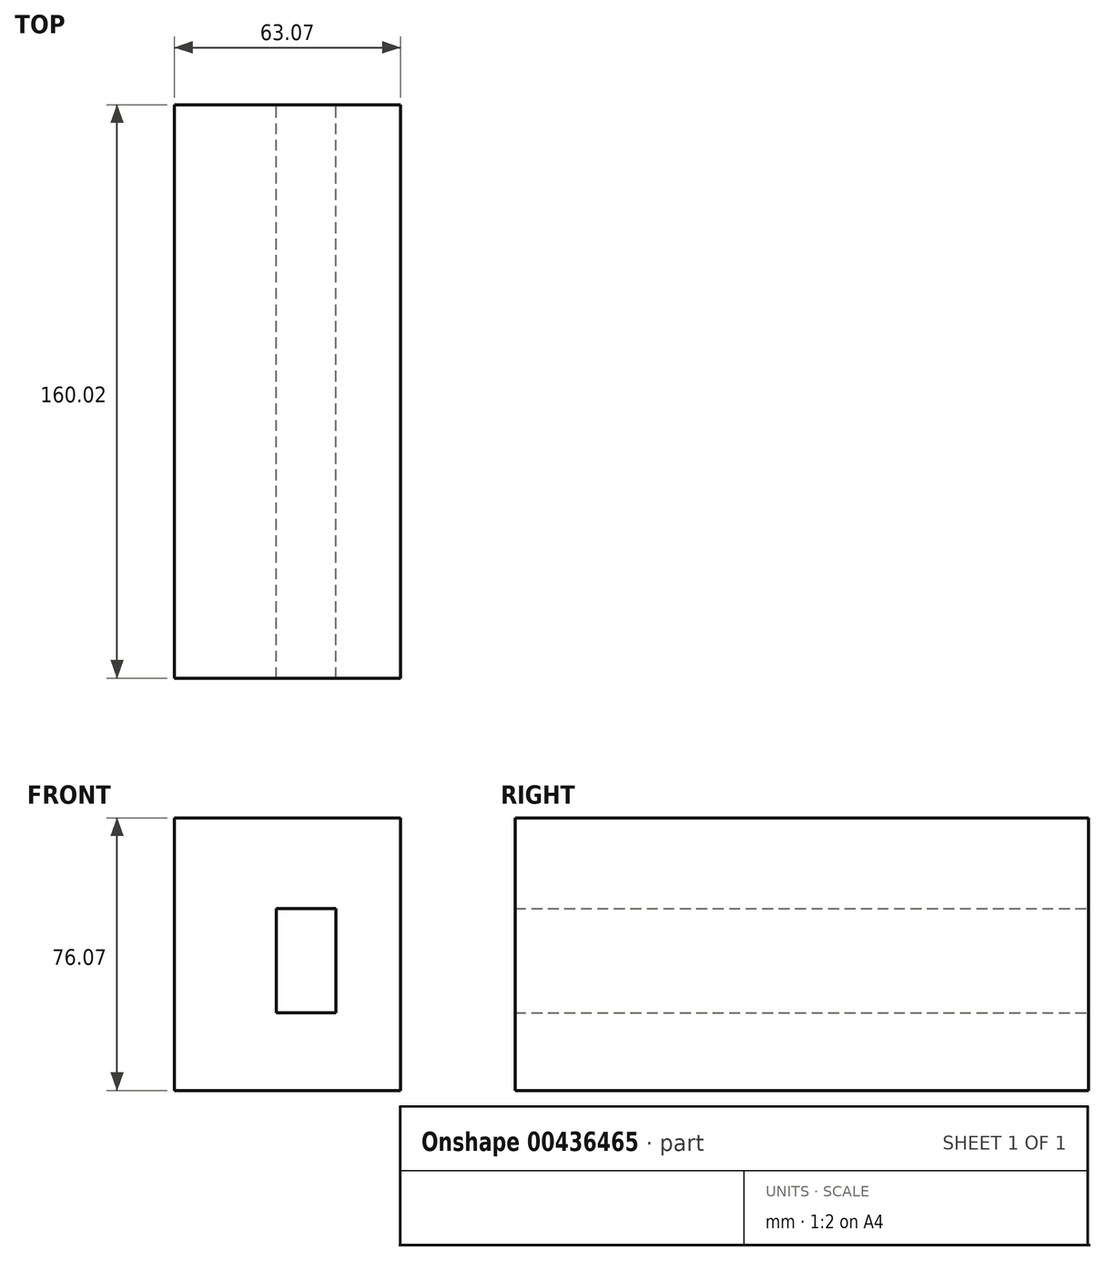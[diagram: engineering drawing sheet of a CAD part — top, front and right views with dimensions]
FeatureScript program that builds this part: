
annotation { "Feature Type Name" : "Feature", "Feature Type Description" : "" }
export const myFeature = defineFeature(function(context is Context, id is Id, definition is map)
    precondition{}
    {
        {
            var Q0;
            Q0=qCreatedBy(makeId("Front.planeOp"),FACE);
            var sketch = newSketch(context, id + "F0", { "sketchPlane" : qUnion([Q0])});
            skLineSegment(sketch, "E0.bottom", {"start": v(-45.1, 45.99) * mm, "end": v(17.97, 45.99) * mm});
            skLineSegment(sketch, "E0.top", {"start": v(-45.1, -30.08) * mm, "end": v(17.97, -30.08) * mm});
            skLineSegment(sketch, "E0.left", {"start": v(-45.1, 45.99) * mm, "end": v(-45.1, -30.08) * mm});
            skLineSegment(sketch, "E0.right", {"start": v(17.97, 45.99) * mm, "end": v(17.97, -30.08) * mm});
            skLineSegment(sketch, "E1.bottom", {"start": v(-16.62, 20.64) * mm, "end": v(0, 20.64) * mm});
            skLineSegment(sketch, "E1.top", {"start": v(-16.62, -8.38) * mm, "end": v(0, -8.38) * mm});
            skLineSegment(sketch, "E1.left", {"start": v(-16.62, 20.64) * mm, "end": v(-16.62, -8.38) * mm});
            skLineSegment(sketch, "E1.right", {"start": v(0, 20.64) * mm, "end": v(0, -8.38) * mm});
            skSolve(sketch);
        }
        {
            var Q0;
            Q0=makeQuery(id+"F0.imprint","IMPRINT",FACE,{"disambiguationData":[TD([[makeQuery(id+"F0.imprint","IMPRINT",EDGE,{"derivedFrom":sQuery(id+"F0.wireOp",EDGE,"E0.bottom")}),-1.0]])]});
            extrude(context, id + "F1", {"entities" : qUnion([Q0]), "depth" : 160.02 * mm});
        }
    });
